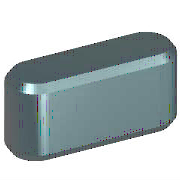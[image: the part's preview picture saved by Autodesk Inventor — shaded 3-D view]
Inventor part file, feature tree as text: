
AUTODESK INVENTOR PART (.ipt)
format: ipt  version: 2025 (Build 290162000, 162)  size: 151,040 bytes
history: native  units: mm (DEFAULTED — no unit token found)
features: other x2, extrude x1, plane x1, hole x1
ambient origin geometry x8: Origin, YZ Plane, XZ Plane, XY Plane, X Axis, Y Axis, Z Axis, Center Point
bodies: Solid1 (feature_tree)
feature tree (5):
  other  "IDS_WORKPLANE{1}"
  other  "IDS_WORKPLANE{2}"
  extrude  "轴承体1"  Depth=9.0mm
  plane  "Work Plane3"
  hole  "螺纹1"  [1 undecoded]
note: 1 required parameter value undecoded (feature->parameter linkage not recoverable at this tier; creation-order binding heuristic only, values carry confidence <= 0.55)
